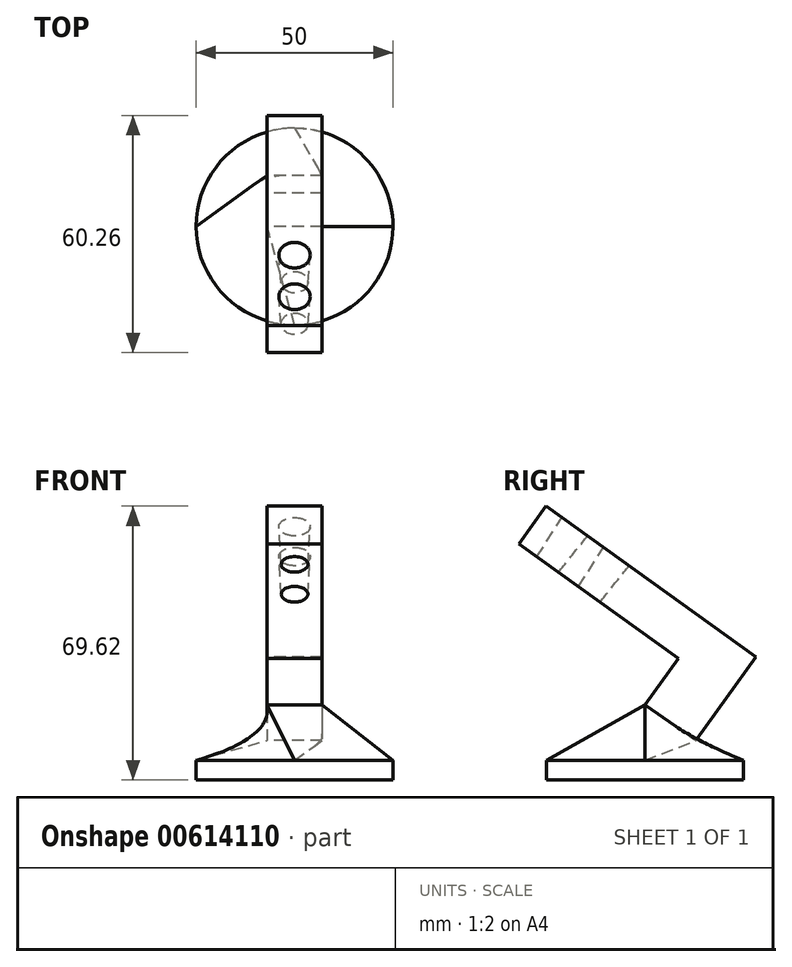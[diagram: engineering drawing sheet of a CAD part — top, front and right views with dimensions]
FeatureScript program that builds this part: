
annotation { "Feature Type Name" : "Feature", "Feature Type Description" : "" }
export const myFeature = defineFeature(function(context is Context, id is Id, definition is map)
    precondition{}
    {
        {
            var Q0;
            Q0=qCreatedBy(makeId("Right.planeOp"),FACE);
            var sketch = newSketch(context, id + "F0", { "sketchPlane" : qUnion([Q0])});
            skLineSegment(sketch, "E0", {"start": v(0, 9.14) * mm, "end": v(8.48, 20.94) * mm});
            skLineSegment(sketch, "E1", {"start": v(8.48, 20.94) * mm, "end": v(-32.06, 50.05) * mm});
            skLineSegment(sketch, "E2", {"start": v(-32.06, 50.05) * mm, "end": v(-25.18, 59.62) * mm});
            skLineSegment(sketch, "E3", {"start": v(-25.18, 59.62) * mm, "end": v(28.2, 21.28) * mm});
            skLineSegment(sketch, "E4", {"start": v(28.2, 21.28) * mm, "end": v(12.96, 0.07) * mm});
            skLineSegment(sketch, "E5", {"start": v(0, 9.14) * mm, "end": v(12.96, 0.07) * mm});
            skSolve(sketch);
        }
        {
            var Q0;
            Q0 = qSketchRegion(id + "F0", true);
            extrude(context, id + "F1", {"entities" : qUnion([Q0]), "depth" : 7 * mm, "offsetDistance" : 25 * mm, "hasSecondDirection" : true, "secondDirectionOppositeDirection" : true, "secondDirectionDepth" : 7 * mm});
        }
        {
            var Q0;
            Q0=makeQuery(id+"F1.opExtrude","SWEPT_FACE",FACE,{"disambiguationData":[OSD([sQuery(id+"F0.wireOp",EDGE,"E3")])]});
            var sketch = newSketch(context, id + "F2", { "sketchPlane" : qUnion([Q0])});
            skCircle(sketch, "E6", {"center": v(0, -33.23) * mm, "radius": 4 * mm});
            skCircle(sketch, "E7", {"center": v(0, -46.23) * mm, "radius": 4 * mm});
            skSolve(sketch);
        }
        {
            var Q0;
            Q0=makeQuery(id+"F2.imprint","IMPRINT",FACE,{"disambiguationData":[TD([[makeQuery(id+"F2.imprint","IMPRINT",EDGE,{"derivedFrom":sQuery(id+"F2.wireOp",EDGE,"E6")}),1.0]])]});
            var Q1;
            Q1=makeQuery(id+"F2.imprint","IMPRINT",FACE,{"disambiguationData":[TD([[makeQuery(id+"F2.imprint","IMPRINT",EDGE,{"derivedFrom":sQuery(id+"F2.wireOp",EDGE,"E7")}),1.0]])]});
            extrude(context, id + "F3", {"entities" : qUnion([Q0, Q1]), "operationType" : NewBodyOperationType.REMOVE, "oppositeDirection" : true, "depth" : 19 * mm, "offsetDistance" : 25 * mm, "hasDraft" : true, "draftAngle" : 3 * degree, "draftPullDirection" : true});
        }
        {
            var Q0;
            Q0=qCreatedBy(makeId("Top.planeOp"),FACE);
            cPlane(context, id + "F4", {"entities" : qUnion([Q0]), "cplaneType" : CPlaneType.OFFSET, "offset" : 10 * mm, "oppositeDirection" : true, "width" : 150 * mm, "height" : 150 * mm});
        }
        {
            var Q0;
            Q0=qCreatedBy(id+"F4.planeOp",FACE);
            var sketch = newSketch(context, id + "F5", { "sketchPlane" : qUnion([Q0])});
            skCircle(sketch, "E8", {"center": v(0, 0) * mm, "radius": 25 * mm});
            skSolve(sketch);
        }
        {
            var Q0;
            Q0=makeQuery(id+"F5.imprint","IMPRINT",FACE,{"disambiguationData":[TD([[makeQuery(id+"F5.imprint","IMPRINT",EDGE,{"derivedFrom":sQuery(id+"F5.wireOp",EDGE,"E8")}),1.0]])]});
            extrude(context, id + "F6", {"entities" : qUnion([Q0]), "depth" : 5 * mm, "offsetDistance" : 25 * mm});
        }
        {
            var Q1;
            Q1=makeQuery(id+"F6.opExtrude","CAP_FACE",FACE,{"disambiguationData":[OSD([sQuery(id+"F5.wireOp",EDGE,"E8")])],"isStart":false});
            var Q2;
            Q2=makeQuery(id+"F1.opExtrude","SWEPT_FACE",FACE,{"disambiguationData":[OSD([sQuery(id+"F0.wireOp",EDGE,"E5")])]});
            loft(context, id + "F7", {"operationType" : NewBodyOperationType.ADD, "sheetProfilesArray" : [{ "sheetProfileEntities" : qUnion([Q1]) }, { "sheetProfileEntities" : qUnion([Q2]) }]});
        }
    });
